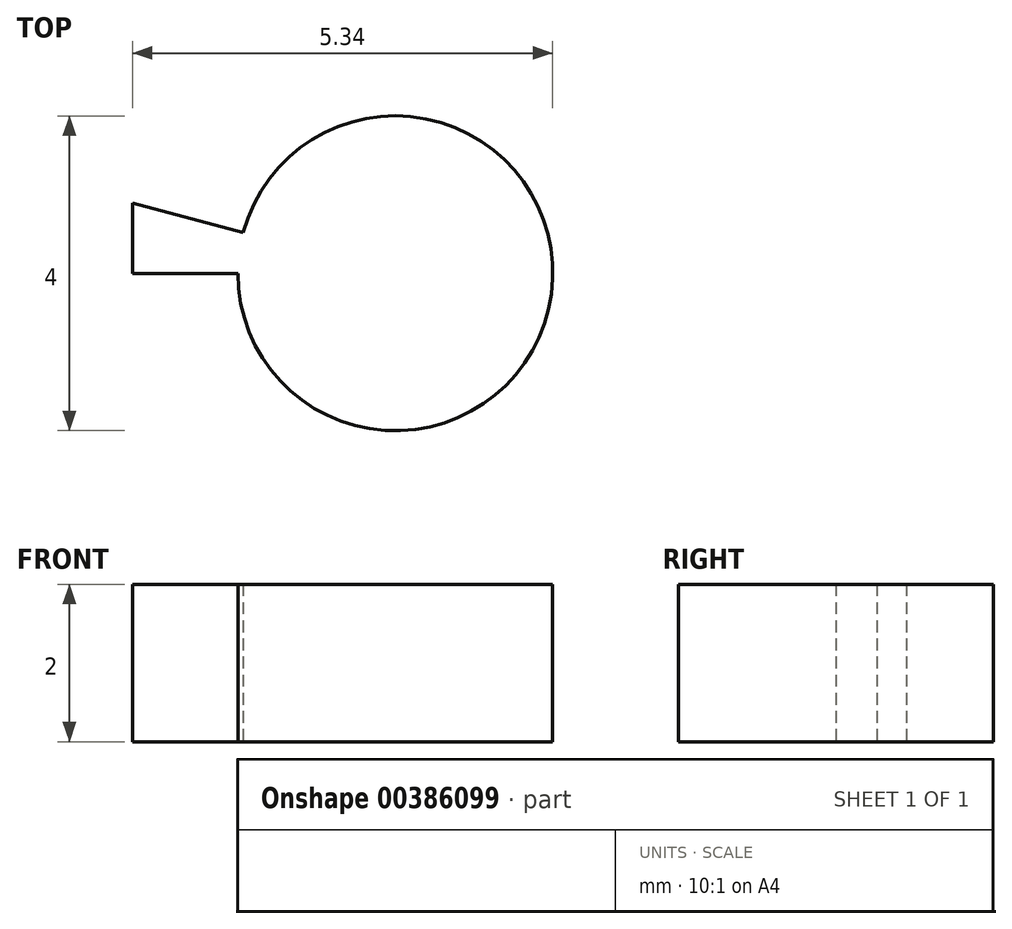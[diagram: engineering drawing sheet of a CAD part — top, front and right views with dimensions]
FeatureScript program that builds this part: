
annotation { "Feature Type Name" : "Feature", "Feature Type Description" : "" }
export const myFeature = defineFeature(function(context is Context, id is Id, definition is map)
    precondition{}
    {
        {
            var Q0;
            Q0=qCreatedBy(makeId("Top.planeOp"),FACE);
            var sketch = newSketch(context, id + "F0", { "sketchPlane" : qUnion([Q0])});
            skLineSegment(sketch, "E0", {"start": v(0, 0) * mm, "end": v(-3.34, 0) * mm});
            skLineSegment(sketch, "E1", {"start": v(-3.34, 0) * mm, "end": v(-3.34, 0.9) * mm});
            skLineSegment(sketch, "E2", {"start": v(-3.34, 0.9) * mm, "end": v(0, 0) * mm});
            skArc(sketch, "E3", {"start": v(-2, 0) * mm, "mid": v(1.98, -0.26) * mm, "end": v(-1.93, 0.52) * mm});
            skSolve(sketch);
        }
        {
            var Q0;
            Q0 = qSketchRegion(id + "F0", true);
            extrude(context, id + "F1", {"entities" : qUnion([Q0]), "depth" : 2 * mm});
        }
    });
